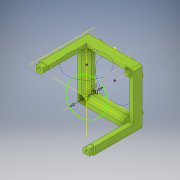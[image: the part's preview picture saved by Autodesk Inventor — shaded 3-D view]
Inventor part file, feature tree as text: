
AUTODESK INVENTOR PART (.ipt)
format: ipt  version: 2019 (Build 230136000, 136)  size: 563,712 bytes
history: native  units: mm
features: projected_geometry x16, sketch x14, extrude x11, plane x6, other x5, hole x3, fillet x2
ambient origin geometry x8: Origin, YZ Plane, XZ Plane, XY Plane, X Axis, Y Axis, Z Axis, Center Point
bodies: Solid1 (feature_tree)
feature tree (57):
  extrude  "Extrusion1"  Depth=49.7mm
  extrude  "Extrusion2"  Depth=8.0mm TaperAngle=0.0deg
  hole  "Hole1"  [1 undecoded]
  sketch  "Sketch4"  dims[d8=3.1mm d9=6.0mm d10=5.5mm d11=4.6mm d12=90.0deg d13=16.0mm d14=20.594885mm d23=2.0mm d30=33.8mm d31=0.0mm]
  sketch  "Sketch5"  dims[d35=33.8mm d36=0.0mm d39=53.8mm]
  other  "Work Axis1"
  other  "Work Axis2"
  fillet  "Fillet1"  Radius=33.8mm
  extrude  "Extrusion3"  Depth=53.8mm
  extrude  "Extrusion4"  Depth=2.0mm
  plane  "Work Plane1"
  extrude  "Extrusion5"  Depth=3.65mm
  hole  "Hole2"  [1 undecoded]
  extrude  "Extrusion6"  Depth=3.65mm
  extrude  "Extrusion7"  Depth=3.78mm
  extrude  "Extrusion8"  Depth=3.78mm
  fillet  "Fillet2"  Radius=3.78mm
  extrude  "Extrusion9"  Depth=10.0mm TaperAngle=0.0deg
  extrude  "Extrusion10"  Depth=4.2mm TaperAngle=0.0deg
  plane  "Work Plane2"
  plane  "Work Plane3"
  hole  "Hole9"  [1 undecoded]
  extrude  "Extrusion11"  Depth=3.4mm
  other  "Work Axis18"
  plane  "Work Plane4"
  sketch  "Sketch23"  dims[d124=3.7mm d125=0.0mm d130=4.2mm d131=0.0mm d132=2.0mm d133=0.5mm d134=3.4mm d135=21.0mm d136=7.38mm d137=3.69mm d138=40.0mm d140=360.0deg d142=4.0mm d143=0.0mm d144=4.95mm d145=2.05mm d146=5.5mm d147=40.0mm d149=360.0deg d151=2.2mm d152=0.0mm d153=3.1mm d154=6.0mm d155=5.5mm d156=3.2mm d157=90.0deg d158=16.0mm d159=20.594885mm d160=5.5mm d161=90.0deg d162=10.0mm d163=0.0mm d164=3.1mm d169=6.1mm d170=6.1mm d171=6.1mm d172=6.1mm d173=1.1mm d174=1.1mm d175=3.78mm d176=3.78mm d177=4.18mm d178=4.18mm d179=4.18mm d180=4.18mm d181=4.18mm d182=4.18mm d183=4.18mm d184=30.0mm d185=0.2mm d186=0.2mm]
  other  "Work Axis19"
  sketch  "Sketch1"  dims[d0=49.7mm d1=49.7mm]
  sketch  "Sketch2"  dims[d2=7.88mm d3=8.0mm d4=0.0mm]
  projected_geometry  "Projected Loop1"
  sketch  "Sketch3"  dims[d5=34.1mm d6=0.0mm]
  projected_geometry  "Projected Loop3"
  projected_geometry  "Projected Loop4"
  projected_geometry  "Projected Loop5"
  projected_geometry  "Projected Loop6"
  projected_geometry  "Projected Loop7"
  sketch  "Sketch9"  dims[d40=33.8mm d41=0.0mm]
  sketch  "Sketch16"  dims[d42=2.8mm d43=6.0mm d44=3.0mm d45=2.0mm d46=90.0deg d47=12.0mm d48=20.594885mm d96=3.65mm]
  projected_geometry  "Projected Loop14"
  projected_geometry  "Projected Loop15"
  sketch  "Sketch17"  dims[d97=3.65mm d98=3.65mm]
  projected_geometry  "Projected Loop16"
  projected_geometry  "Projected Loop17"
  sketch  "Sketch18"  dims[d99=3.65mm d100=3.65mm]
  sketch  "Sketch19"  dims[d101=3.65mm d102=3.65mm]
  projected_geometry  "Projected Loop22"
  sketch  "Sketch20"  dims[d105=3.78mm d106=3.78mm]
  projected_geometry  "Projected Loop23"
  sketch  "Sketch21"  dims[d107=3.78mm d109=3.78mm d110=3.78mm]
  projected_geometry  "Projected Loop24"
  sketch  "Sketch22"  dims[d112=45.0deg d120=10.0mm d121=0.0mm]
  projected_geometry  "Projected Loop25"
  projected_geometry  "Projected Loop28"
  projected_geometry  "Projected Loop29"
  other  "Work Point1"
  plane  "Work Plane5"
  plane  "Work Plane6"
note: 3 required parameter values undecoded (feature->parameter linkage not recoverable at this tier; creation-order binding heuristic only, values carry confidence <= 0.55)
